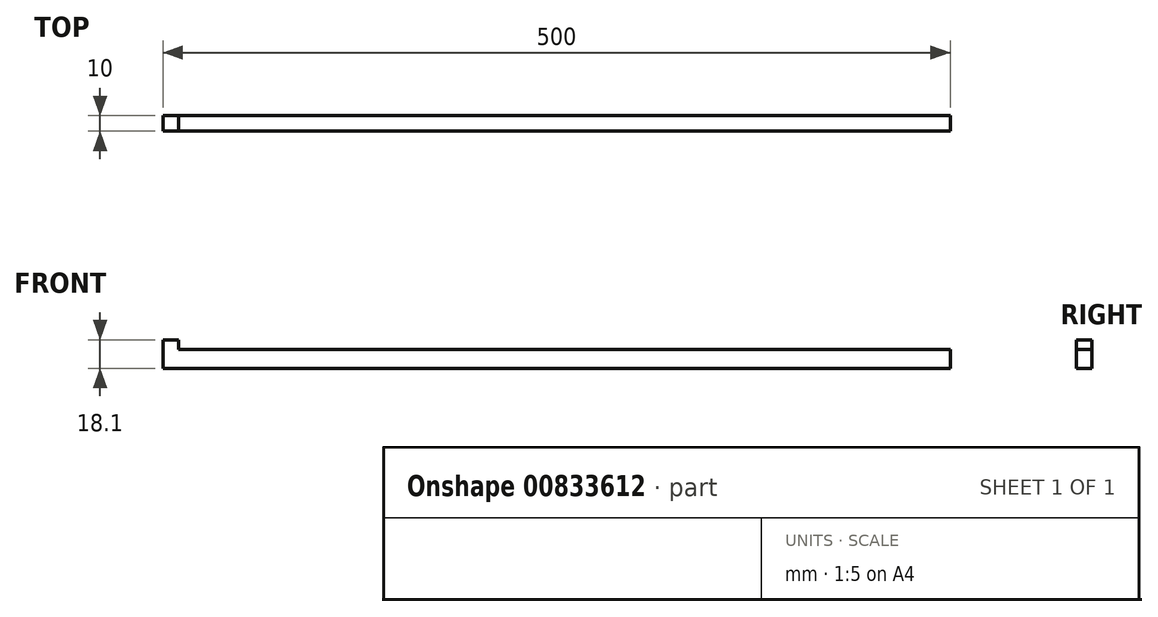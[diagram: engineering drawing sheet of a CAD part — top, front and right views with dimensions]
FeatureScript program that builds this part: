
annotation { "Feature Type Name" : "Feature", "Feature Type Description" : "" }
export const myFeature = defineFeature(function(context is Context, id is Id, definition is map)
    precondition{}
    {
        {
            var Q0;
            Q0=qCreatedBy(makeId("Right.planeOp"),FACE);
            var sketch = newSketch(context, id + "F0", { "sketchPlane" : qUnion([Q0])});
            skLineSegment(sketch, "E0.bottom", {"start": v(5, 6) * mm, "end": v(-5, 6) * mm});
            skLineSegment(sketch, "E0.top", {"start": v(5, -6) * mm, "end": v(-5, -6) * mm});
            skLineSegment(sketch, "E0.left", {"start": v(5, 6) * mm, "end": v(5, -6) * mm});
            skLineSegment(sketch, "E0.right", {"start": v(-5, 6) * mm, "end": v(-5, -6) * mm});
            skPoint(sketch, "E0.middle", {"position": v(0, 0) * mm});
            skSolve(sketch);
        }
        {
            var Q0;
            Q0 = qSketchRegion(id + "F0", true);
            var Q1;
            Q1=makeQuery(id+"F0.imprint","IMPRINT",FACE,{"disambiguationData":[TD([[makeQuery(id+"F0.imprint","IMPRINT",EDGE,{"derivedFrom":sQuery(id+"F0.wireOp",EDGE,"E0.bottom")}),1.0]])]});
            extrude(context, id + "F1", {"entities" : qUnion([Q0, Q1]), "depth" : 500 * mm, "offsetDistance" : 25 * mm});
        }
        {
            var Q0;
            Q0=makeQuery(id+"F1.opExtrude","SWEPT_FACE",FACE,{"disambiguationData":[OSD([sQuery(id+"F0.wireOp",EDGE,"E0.bottom")])]});
            var sketch = newSketch(context, id + "F2", { "sketchPlane" : qUnion([Q0])});
            skLineSegment(sketch, "E1.bottom", {"start": v(0, 5) * mm, "end": v(10, 5) * mm});
            skLineSegment(sketch, "E1.top", {"start": v(0, -5) * mm, "end": v(10, -5) * mm});
            skLineSegment(sketch, "E1.left", {"start": v(0, 5) * mm, "end": v(0, -5) * mm});
            skLineSegment(sketch, "E1.right", {"start": v(10, 5) * mm, "end": v(10, -5) * mm});
            skSolve(sketch);
        }
        {
            var Q0;
            Q0=makeQuery(id+"F2.imprint","IMPRINT",FACE,{"disambiguationData":[TD([[makeQuery(id+"F2.imprint","IMPRINT",EDGE,{"derivedFrom":sQuery(id+"F2.wireOp",EDGE,"E1.bottom")}),1.0]])]});
            extrude(context, id + "F3", {"entities" : qUnion([Q0]), "operationType" : NewBodyOperationType.ADD, "depth" : 6.1 * mm, "offsetDistance" : 25 * mm});
        }
    });
